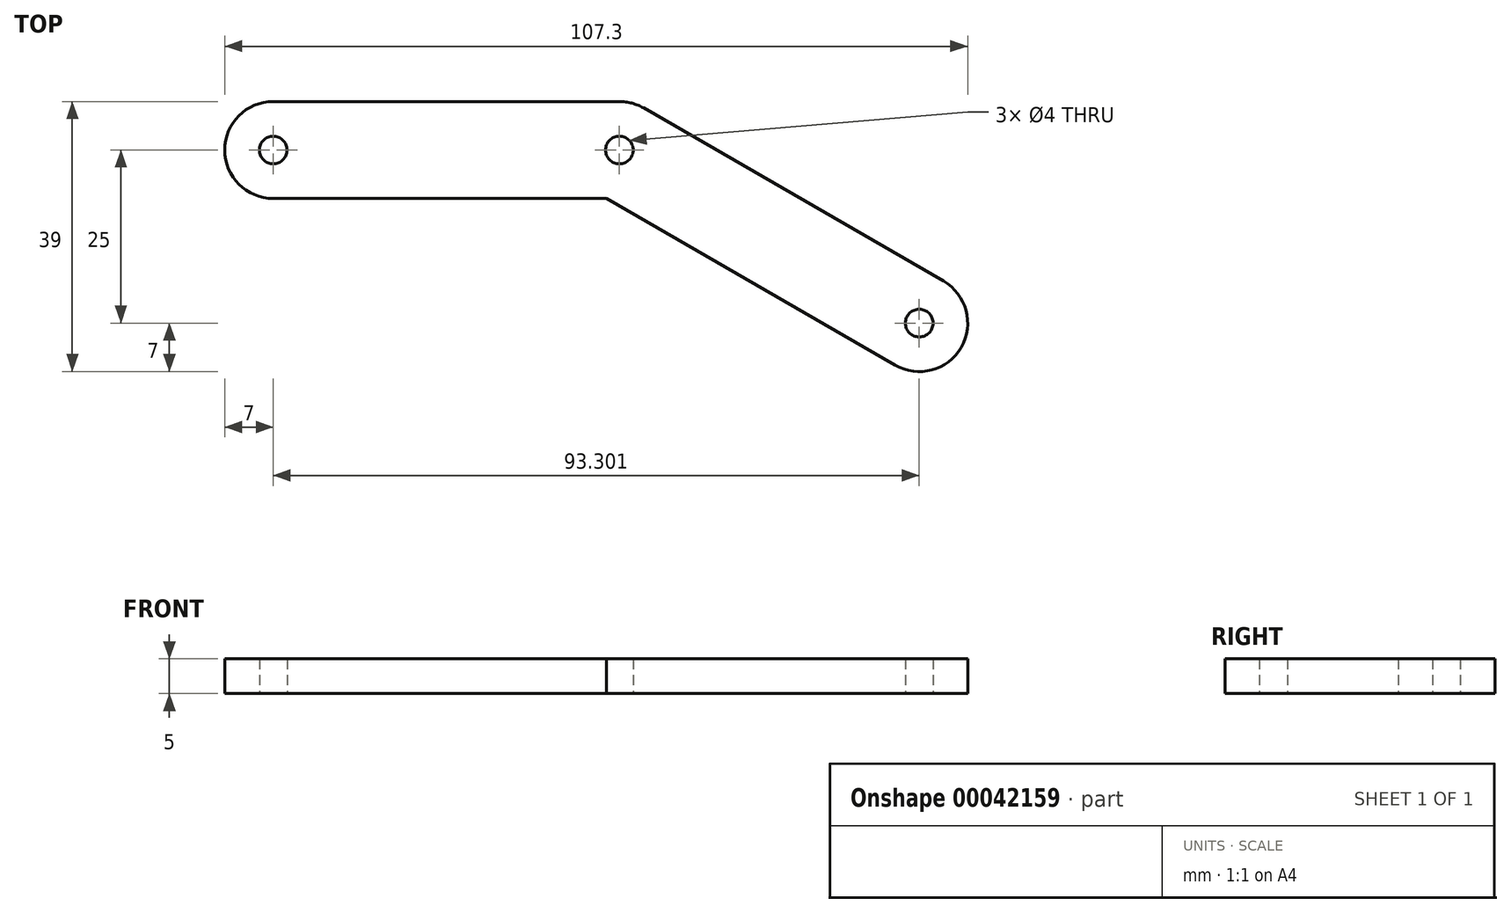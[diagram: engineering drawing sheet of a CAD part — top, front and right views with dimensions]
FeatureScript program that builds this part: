
annotation { "Feature Type Name" : "Feature", "Feature Type Description" : "" }
export const myFeature = defineFeature(function(context is Context, id is Id, definition is map)
    precondition{}
    {
        {
            var Q0;
            Q0=qCreatedBy(makeId("Top.planeOp"),FACE);
            var sketch = newSketch(context, id + "F0", { "sketchPlane" : qUnion([Q0])});
            skCircle(sketch, "E0", {"center": v(-50, 0) * mm, "radius": 2 * mm});
            skCircle(sketch, "E1", {"center": v(0, 0) * mm, "radius": 2 * mm});
            skCircle(sketch, "E2", {"center": v(43.3, -25) * mm, "radius": 2 * mm});
            skLineSegment(sketch, "E3", {"start": v(-50, 0) * mm, "end": v(0, 0) * mm, "construction": true});
            skLineSegment(sketch, "E4", {"start": v(0, 0) * mm, "end": v(43.3, -25) * mm, "construction": true});
            skArc(sketch, "E5.0.startCap", {"start": v(-50, -7) * mm, "mid": v(-57, 0) * mm, "end": v(-50, 7) * mm});
            skArc(sketch, "E5.0.endCap", {"start": v(0, 7) * mm, "mid": v(1.81, 6.76) * mm, "end": v(3.5, 6.06) * mm});
            skLineSegment(sketch, "E5.0.left", {"start": v(-50, 7) * mm, "end": v(0, 7) * mm});
            skLineSegment(sketch, "E5.0.right", {"start": v(-50, -7) * mm, "end": v(-1.88, -7) * mm});
            skArc(sketch, "E5.1.endCap", {"start": v(46.8, -18.94) * mm, "mid": v(49.36, -28.5) * mm, "end": v(39.8, -31.06) * mm});
            skLineSegment(sketch, "E5.1.left", {"start": v(3.5, 6.06) * mm, "end": v(46.8, -18.94) * mm});
            skLineSegment(sketch, "E5.1.right", {"start": v(-1.88, -7) * mm, "end": v(39.8, -31.06) * mm});
            skSolve(sketch);
        }
        {
            var Q0;
            Q0=makeQuery(id+"F0.imprint","IMPRINT",FACE,{"disambiguationData":[TD([[makeQuery(id+"F0.imprint","IMPRINT",EDGE,{"derivedFrom":sQuery(id+"F0.wireOp",EDGE,"E0")}),-1.0]])]});
            extrude(context, id + "F1", {"entities" : qUnion([Q0]), "depth" : 5 * mm});
        }
    });
